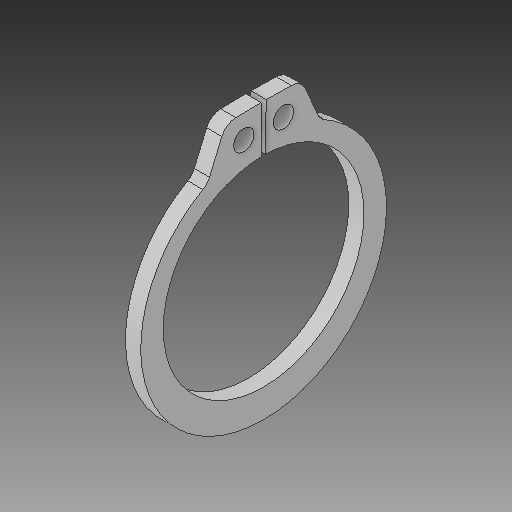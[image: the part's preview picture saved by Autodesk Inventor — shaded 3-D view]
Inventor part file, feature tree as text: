
AUTODESK INVENTOR PART (.ipt)
format: ipt  version: 2018 (Build 220112000, 112)  size: 110,592 bytes
history: native  units: in
note: dims shown in document units (in); Inventor stores cm internally (conversion verified against a paired STEP export)
features: fillet x1
ambient origin geometry x8: Origin, YZ Plane, XZ Plane, XY Plane, X Axis, Y Axis, Z Axis, Center Point
bodies: Solid1 (feature_tree)
feature tree (1):
  fillet  "Fillet1"  [1 undecoded]
note: 1 required parameter value undecoded (feature->parameter linkage not recoverable at this tier; creation-order binding heuristic only, values carry confidence <= 0.55)
